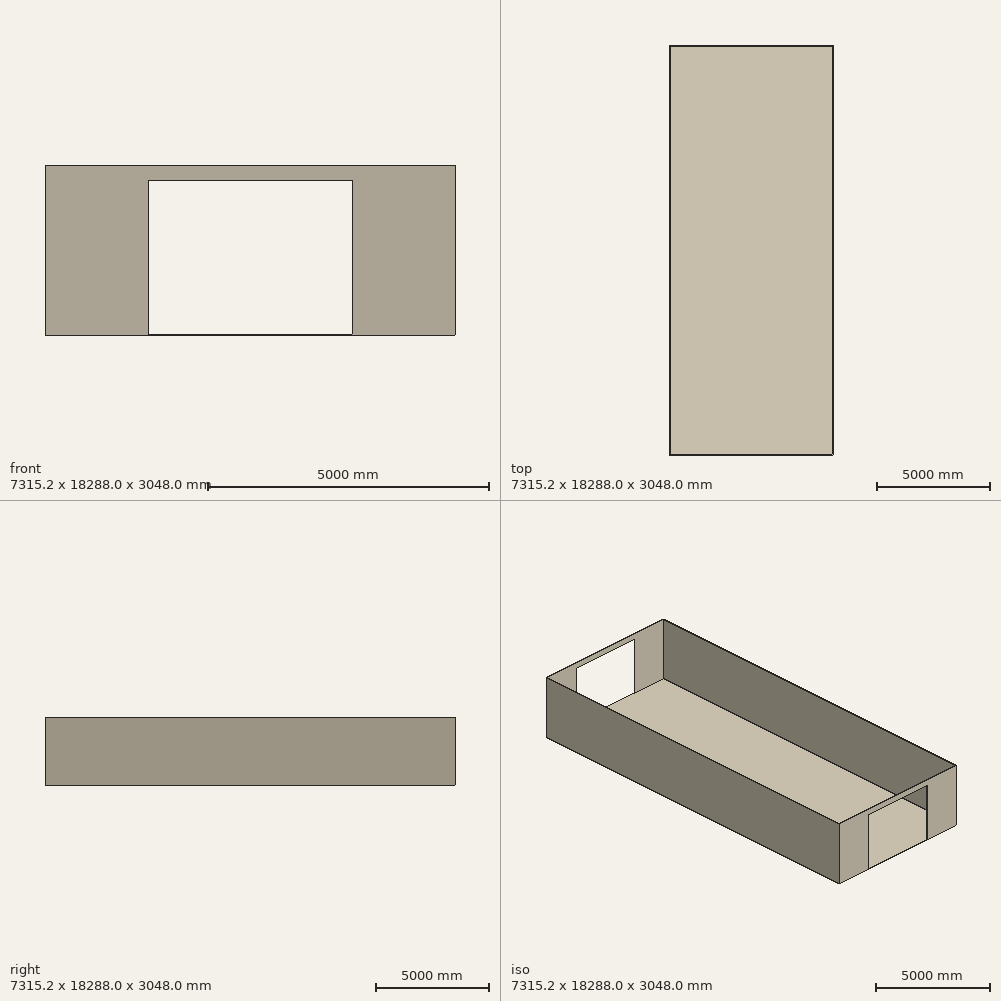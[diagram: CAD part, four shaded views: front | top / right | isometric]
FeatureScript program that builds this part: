
annotation { "Feature Type Name" : "Feature", "Feature Type Description" : "" }
export const myFeature = defineFeature(function(context is Context, id is Id, definition is map)
    precondition{}
    {
        {
            var Q0;
            Q0=qCreatedBy(makeId("Top.planeOp"),FACE);
            var sketch = newSketch(context, id + "F0", { "sketchPlane" : qUnion([Q0])});
            skLineSegment(sketch, "E0.bottom", {"start": v(-3657.6, 9144) * mm, "end": v(3657.6, 9144) * mm});
            skLineSegment(sketch, "E0.top", {"start": v(-3657.6, -9144) * mm, "end": v(3657.6, -9144) * mm});
            skLineSegment(sketch, "E0.left", {"start": v(-3657.6, 9144) * mm, "end": v(-3657.6, -9144) * mm});
            skLineSegment(sketch, "E0.right", {"start": v(3657.6, 9144) * mm, "end": v(3657.6, -9144) * mm});
            skSolve(sketch);
        }
        {
            var Q0;
            Q0=makeQuery(id+"F0.imprint","IMPRINT",FACE,{"disambiguationData":[TD([[makeQuery(id+"F0.imprint","IMPRINT",EDGE,{"derivedFrom":sQuery(id+"F0.wireOp",EDGE,"E0.bottom")}),-1.0]])]});
            extrude(context, id + "F1", {"entities" : qUnion([Q0]), "depth" : 3048 * mm});
        }
        {
            var Q0;
            Q0=makeQuery(id+"F1.opExtrude","CAP_FACE",FACE,{"disambiguationData":[OSD([sQuery(id+"F0.wireOp",EDGE,"E0.bottom"),sQuery(id+"F0.wireOp",EDGE,"E0.top"),sQuery(id+"F0.wireOp",EDGE,"E0.left"),sQuery(id+"F0.wireOp",EDGE,"E0.right")])],"isStart":false});
            var sketch = newSketch(context, id + "F2", { "sketchPlane" : qUnion([Q0])});
            skLineSegment(sketch, "E1.bottom", {"start": v(-3632.2, 9118.6) * mm, "end": v(3632.2, 9118.6) * mm});
            skLineSegment(sketch, "E1.top", {"start": v(-3632.2, -9118.6) * mm, "end": v(3632.2, -9118.6) * mm});
            skLineSegment(sketch, "E1.left", {"start": v(-3632.2, 9118.6) * mm, "end": v(-3632.2, -9118.6) * mm});
            skLineSegment(sketch, "E1.right", {"start": v(3632.2, 9118.6) * mm, "end": v(3632.2, -9118.6) * mm});
            skSolve(sketch);
        }
        {
            var Q0;
            Q0 = qSketchRegion(id + "F2", true);
            extrude(context, id + "F3", {"entities" : qUnion([Q0]), "operationType" : NewBodyOperationType.REMOVE, "oppositeDirection" : true, "depth" : 3022.6 * mm});
        }
        {
            var Q0;
            Q0=makeQuery(id+"F1.opExtrude","SWEPT_FACE",FACE,{"disambiguationData":[OSD([sQuery(id+"F0.wireOp",EDGE,"E0.top")])]});
            var sketch = newSketch(context, id + "F4", { "sketchPlane" : qUnion([Q0])});
            skLineSegment(sketch, "E2.bottom", {"start": v(-1828.8, 2768.6) * mm, "end": v(1828.8, 2768.6) * mm});
            skLineSegment(sketch, "E2.top", {"start": v(-1828.8, 25.4) * mm, "end": v(1828.8, 25.4) * mm});
            skLineSegment(sketch, "E2.left", {"start": v(-1828.8, 2768.6) * mm, "end": v(-1828.8, 25.4) * mm});
            skLineSegment(sketch, "E2.right", {"start": v(1828.8, 2768.6) * mm, "end": v(1828.8, 25.4) * mm});
            skSolve(sketch);
        }
        {
            var Q0;
            Q0=makeQuery(id+"F4.imprint","IMPRINT",FACE,{"disambiguationData":[TD([[makeQuery(id+"F4.imprint","IMPRINT",EDGE,{"derivedFrom":sQuery(id+"F4.wireOp",EDGE,"E2.bottom")}),-1.0]])]});
            extrude(context, id + "F5", {"entities" : qUnion([Q0]), "operationType" : NewBodyOperationType.REMOVE, "oppositeDirection" : true, "depth" : 20320 * mm});
        }
    });
